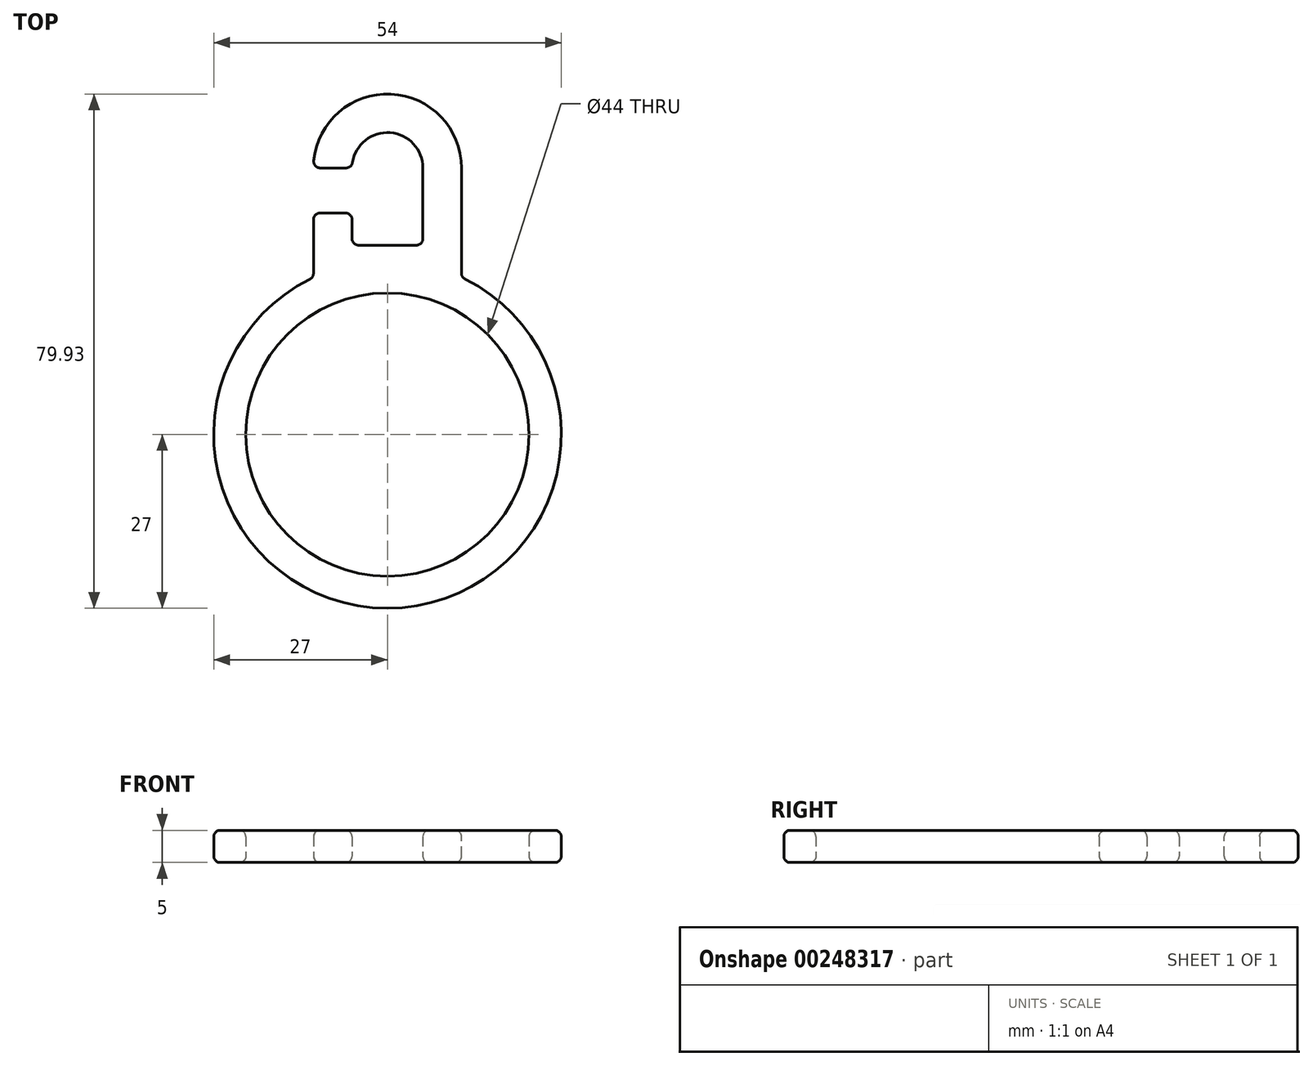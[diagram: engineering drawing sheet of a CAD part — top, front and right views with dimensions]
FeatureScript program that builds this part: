
annotation { "Feature Type Name" : "Feature", "Feature Type Description" : "" }
export const myFeature = defineFeature(function(context is Context, id is Id, definition is map)
    precondition{}
    {
        {
            var Q0;
            Q0=qCreatedBy(makeId("Top.planeOp"),FACE);
            var sketch = newSketch(context, id + "F0", { "sketchPlane" : qUnion([Q0])});
            skCircle(sketch, "E0", {"center": v(0, 0) * mm, "radius": 22 * mm});
            skCircle(sketch, "E1", {"center": v(0, 0) * mm, "radius": 27 * mm});
            skLineSegment(sketch, "E2", {"start": v(-5.5, 34.43) * mm, "end": v(-5.5, 29.43) * mm});
            skLineSegment(sketch, "E3", {"start": v(5.5, 29.43) * mm, "end": v(5.5, 41.43) * mm});
            skArc(sketch, "E4", {"start": v(5.5, 41.43) * mm, "mid": v(0, 46.93) * mm, "end": v(-5.5, 41.43) * mm});
            skLineSegment(sketch, "E5", {"start": v(11.5, 24.43) * mm, "end": v(11.5, 41.43) * mm});
            skLineSegment(sketch, "E6", {"start": v(-11.5, 24.43) * mm, "end": v(-11.5, 34.43) * mm});
            skLineSegment(sketch, "E7", {"start": v(-5.5, 41.43) * mm, "end": v(-11.5, 41.43) * mm});
            skArc(sketch, "E8", {"start": v(11.5, 41.43) * mm, "mid": v(0, 52.93) * mm, "end": v(-11.5, 41.43) * mm});
            skLineSegment(sketch, "E9", {"start": v(-11.5, 34.43) * mm, "end": v(-5.5, 34.43) * mm});
            skLineSegment(sketch, "E10", {"start": v(-5.5, 29.43) * mm, "end": v(5.5, 29.43) * mm});
            skPoint(sketch, "E11.orphan", {"position": v(-5.5, 26.43) * mm});
            skPoint(sketch, "E12.orphan", {"position": v(5.5, 26.43) * mm});
            skSolve(sketch);
        }
        {
            var Q0;
            Q0=makeQuery(id+"F0.imprint","IMPRINT",FACE,{"disambiguationData":[TD([[makeQuery(id+"F0.imprint","IMPRINT",EDGE,{"derivedFrom":sQuery(id+"F0.wireOp",EDGE,"E0")}),-1.0]])]});
            var Q1;
            Q1=makeQuery(id+"F0.imprint","IMPRINT",FACE,{"disambiguationData":[TD([[makeQuery(id+"F0.imprint","IMPRINT",EDGE,{"derivedFrom":sQuery(id+"F0.wireOp",EDGE,"E2")}),-1.0]])]});
            extrude(context, id + "F1", {"entities" : qUnion([Q0, Q1]), "depth" : 5 * mm});
        }
        {
            var Q0;
            Q0=makeQuery(id+"F1.opExtrude","CAP_FACE",FACE,{"disambiguationData":[OSD([sQuery(id+"F0.wireOp",EDGE,"E0"),sQuery(id+"F0.wireOp",EDGE,"E1"),sQuery(id+"F0.wireOp",EDGE,"E2"),sQuery(id+"F0.wireOp",EDGE,"E3"),sQuery(id+"F0.wireOp",EDGE,"E4"),sQuery(id+"F0.wireOp",EDGE,"E5"),sQuery(id+"F0.wireOp",EDGE,"E6"),sQuery(id+"F0.wireOp",EDGE,"E7"),sQuery(id+"F0.wireOp",EDGE,"E8"),sQuery(id+"F0.wireOp",EDGE,"E9"),sQuery(id+"F0.wireOp",EDGE,"E10")])],"isStart":false});
            var Q1;
            Q1=makeQuery(id+"F1.opExtrude","CAP_FACE",FACE,{"disambiguationData":[OSD([sQuery(id+"F0.wireOp",EDGE,"E0"),sQuery(id+"F0.wireOp",EDGE,"E1"),sQuery(id+"F0.wireOp",EDGE,"E2"),sQuery(id+"F0.wireOp",EDGE,"E3"),sQuery(id+"F0.wireOp",EDGE,"E4"),sQuery(id+"F0.wireOp",EDGE,"E5"),sQuery(id+"F0.wireOp",EDGE,"E6"),sQuery(id+"F0.wireOp",EDGE,"E7"),sQuery(id+"F0.wireOp",EDGE,"E8"),sQuery(id+"F0.wireOp",EDGE,"E9"),sQuery(id+"F0.wireOp",EDGE,"E10")])],"isStart":true});
            var Q2;
            Q2=makeQuery(id+"F1.opExtrude","SWEPT_EDGE",EDGE,{"disambiguationData":[OSD([sQuery(id+"F0.wireOp",EDGE,"E1"),sQuery(id+"F0.wireOp",EDGE,"E6")])]});
            var Q3;
            Q3=makeQuery(id+"F1.opExtrude","SWEPT_EDGE",EDGE,{"disambiguationData":[OSD([sQuery(id+"F0.wireOp",EDGE,"E1"),sQuery(id+"F0.wireOp",EDGE,"E5")])]});
            var Q4;
            Q4=makeQuery(id+"F1.opExtrude","SWEPT_EDGE",EDGE,{"disambiguationData":[OSD([sQuery(id+"F0.wireOp",EDGE,"E3"),sQuery(id+"F0.wireOp",EDGE,"E10")])]});
            var Q5;
            Q5=makeQuery(id+"F1.opExtrude","SWEPT_EDGE",EDGE,{"disambiguationData":[OSD([sQuery(id+"F0.wireOp",EDGE,"E2"),sQuery(id+"F0.wireOp",EDGE,"E10")])]});
            var Q6;
            Q6=makeQuery(id+"F1.opExtrude","SWEPT_EDGE",EDGE,{"disambiguationData":[OSD([sQuery(id+"F0.wireOp",EDGE,"E2"),sQuery(id+"F0.wireOp",EDGE,"E9")])]});
            var Q7;
            Q7=makeQuery(id+"F1.opExtrude","SWEPT_EDGE",EDGE,{"disambiguationData":[OSD([sQuery(id+"F0.wireOp",EDGE,"E6"),sQuery(id+"F0.wireOp",EDGE,"E9")])]});
            var Q8;
            Q8=makeQuery(id+"F1.opExtrude","SWEPT_EDGE",EDGE,{"disambiguationData":[OSD([sQuery(id+"F0.wireOp",EDGE,"E4"),sQuery(id+"F0.wireOp",EDGE,"E7")])]});
            var Q9;
            Q9=makeQuery(id+"F1.opExtrude","SWEPT_EDGE",EDGE,{"disambiguationData":[OSD([sQuery(id+"F0.wireOp",EDGE,"E7"),sQuery(id+"F0.wireOp",EDGE,"E8")])]});
            fillet(context, id + "F2", {"entities" : qUnion([Q0, Q1, Q2, Q3, Q4, Q5, Q6, Q7, Q8, Q9]), "radius" : 1 * mm, "tangentPropagation" : true, "allowEdgeOverflow" : false});
        }
    });
